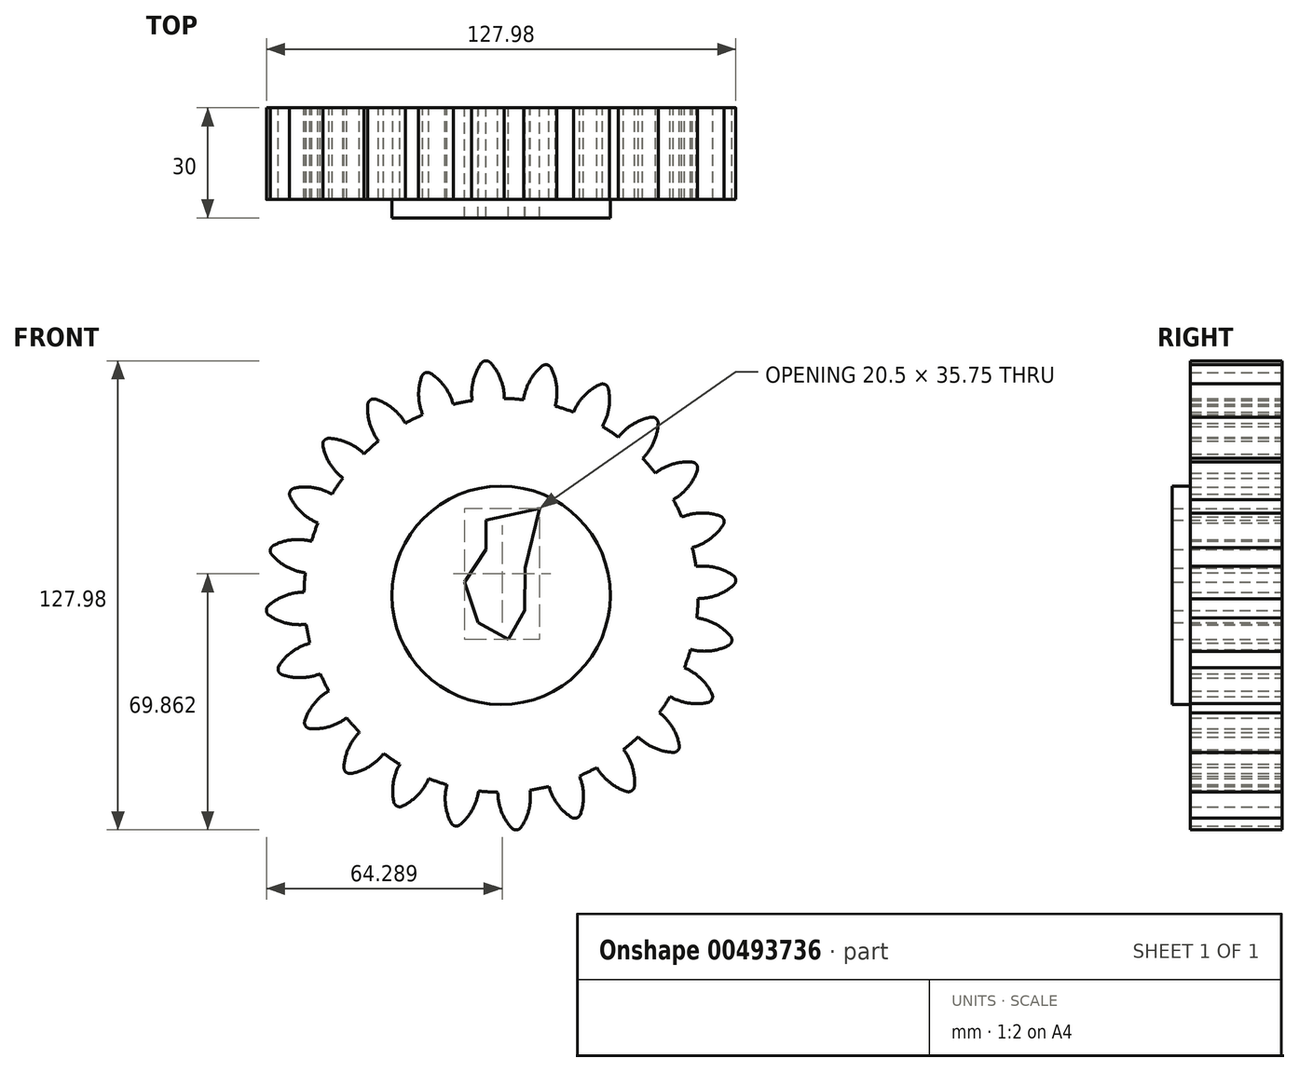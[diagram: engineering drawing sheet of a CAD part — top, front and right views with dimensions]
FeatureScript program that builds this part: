
annotation { "Feature Type Name" : "Feature", "Feature Type Description" : "" }
export const myFeature = defineFeature(function(context is Context, id is Id, definition is map)
    precondition{}
    {
        {
            var Q0;
            Q0=qCreatedBy(makeId("Front.planeOp"),FACE);
            var sketch = newSketch(context, id + "F0", { "sketchPlane" : qUnion([Q0])});
            skCircle(sketch, "E0", {"center": v(0, 0) * mm, "radius": 53.72 * mm});
            skCircle(sketch, "E1", {"center": v(0, 0) * mm, "radius": 58.67 * mm, "construction": true});
            skCircle(sketch, "E2", {"center": v(0, 0) * mm, "radius": 63.5 * mm, "construction": true});
            skLineSegment(sketch, "E3", {"start": v(0, 0) * mm, "end": v(0, 107.47) * mm, "construction": true});
            skLineSegment(sketch, "E4", {"start": v(0, 0) * mm, "end": v(-7.04, 107.47) * mm, "construction": true});
            skLineSegment(sketch, "E5", {"start": v(0, 58.67) * mm, "end": v(-52.69, 58.67) * mm, "construction": true});
            skLineSegment(sketch, "E6", {"start": v(0, 58.67) * mm, "end": v(-51.42, 39.96) * mm, "construction": true});
            skCircle(sketch, "E7", {"center": v(0, 0) * mm, "radius": 55.14 * mm, "construction": true});
            skCircle(sketch, "E8", {"center": v(0, 58.67) * mm, "radius": 14.6 * mm, "construction": true});
            skCircle(sketch, "E9", {"center": v(-13.72, 53.68) * mm, "radius": 14.6 * mm, "construction": true});
            skArc(sketch, "E10", {"start": v(0, 58.67) * mm, "mid": v(-1.2, 61.2) * mm, "end": v(-2.86, 63.44) * mm});
            skArc(sketch, "E11", {"start": v(0.88, 53.71) * mm, "mid": v(0.65, 56.23) * mm, "end": v(0, 58.67) * mm});
            skArc(sketch, "E12.MirrorCS", {"start": v(-7.88, 53.14) * mm, "mid": v(-7.99, 55.67) * mm, "end": v(-7.66, 58.17) * mm});
            skArc(sketch, "E13.MirrorCS", {"start": v(-7.66, 58.17) * mm, "mid": v(-6.8, 60.83) * mm, "end": v(-5.45, 63.27) * mm});
            skArc(sketch, "E14", {"start": v(-2.86, 63.44) * mm, "mid": v(-4.2, 63.99) * mm, "end": v(-5.45, 63.27) * mm});
            skLineSegment(sketch, "E15", {"start": v(-4.07, 12.47) * mm, "end": v(-9.95, 3.57) * mm});
            skLineSegment(sketch, "E16", {"start": v(-9.95, 3.57) * mm, "end": v(-6.3, -7.4) * mm});
            skLineSegment(sketch, "E17", {"start": v(-6.3, -7.4) * mm, "end": v(1.97, -12) * mm});
            skLineSegment(sketch, "E18", {"start": v(1.97, -12) * mm, "end": v(6.38, -4.1) * mm});
            skLineSegment(sketch, "E19", {"start": v(6.38, -4.1) * mm, "end": v(6.57, 7.38) * mm});
            skLineSegment(sketch, "E20", {"start": v(6.57, 7.38) * mm, "end": v(10.55, 23.75) * mm});
            skLineSegment(sketch, "E21", {"start": v(10.55, 23.75) * mm, "end": v(-4.07, 20.57) * mm});
            skLineSegment(sketch, "E22", {"start": v(-4.07, 20.57) * mm, "end": v(-4.07, 12.47) * mm});
            skCircle(sketch, "E23", {"center": v(0, 0) * mm, "radius": 29.8 * mm});
            skSolve(sketch);
        }
        {
            var Q0;
            {var subQ0=sQuery(id+"F0.wireOp",EDGE,"E0");var subQ1=makeQuery(id+"F0.imprint","INTERSECT",VERTEX,{"derivedFrom":[subQ0,sQuery(id+"F0.wireOp",EDGE,"E11")]});Q0=makeQuery(id+"F0.imprint","IMPRINT",FACE,{"disambiguationData":[TD([[makeQuery(id+"F0.imprint","IMPRINT",EDGE,{"disambiguationData":[TD([[subQ1,-1.0]])],"derivedFrom":subQ0}),1.0]])]});}
            var Q1;
            Q1=makeQuery(id+"F0.imprint","IMPRINT",FACE,{"disambiguationData":[TD([[makeQuery(id+"F0.imprint","IMPRINT",EDGE,{"derivedFrom":sQuery(id+"F0.wireOp",EDGE,"E10")}),1.0]])]});
            extrude(context, id + "F1", {"entities" : qUnion([Q0, Q1]), "depth" : 25 * mm, "offsetDistance" : 25 * mm});
        }
        {
            var Q0;
            Q0=makeQuery(id+"F1.opExtrude","SWEPT_BODY",BODY,{"disambiguationData":[OSD([sQuery(id+"F0.wireOp",EDGE,"E0"),sQuery(id+"F0.wireOp",EDGE,"E10"),sQuery(id+"F0.wireOp",EDGE,"E11"),sQuery(id+"F0.wireOp",EDGE,"E12.MirrorCS"),sQuery(id+"F0.wireOp",EDGE,"E13.MirrorCS"),sQuery(id+"F0.wireOp",EDGE,"E14")])]});
            var Q1;
            Q1=makeQuery(id+"F1.opExtrude","SWEPT_FACE",FACE,{"disambiguationData":[OSD([sQuery(id+"F0.wireOp",EDGE,"E0")])]});
            circularPattern(context, id + "F2", {"entities" : qUnion([Q0]), "axis" : qUnion([Q1]), "angle" : 360 * degree, "instanceCount" : 24, "equalSpace" : true});
        }
        {
            var Q0;
            Q0=makeQuery(id+"F0.imprint","IMPRINT",FACE,{"disambiguationData":[TD([[makeQuery(id+"F0.imprint","IMPRINT",EDGE,{"derivedFrom":sQuery(id+"F0.wireOp",EDGE,"E15")}),-1.0]])]});
            extrude(context, id + "F3", {"entities" : qUnion([Q0]), "operationType" : NewBodyOperationType.ADD, "depth" : 30 * mm, "offsetDistance" : 25 * mm});
        }
    });
